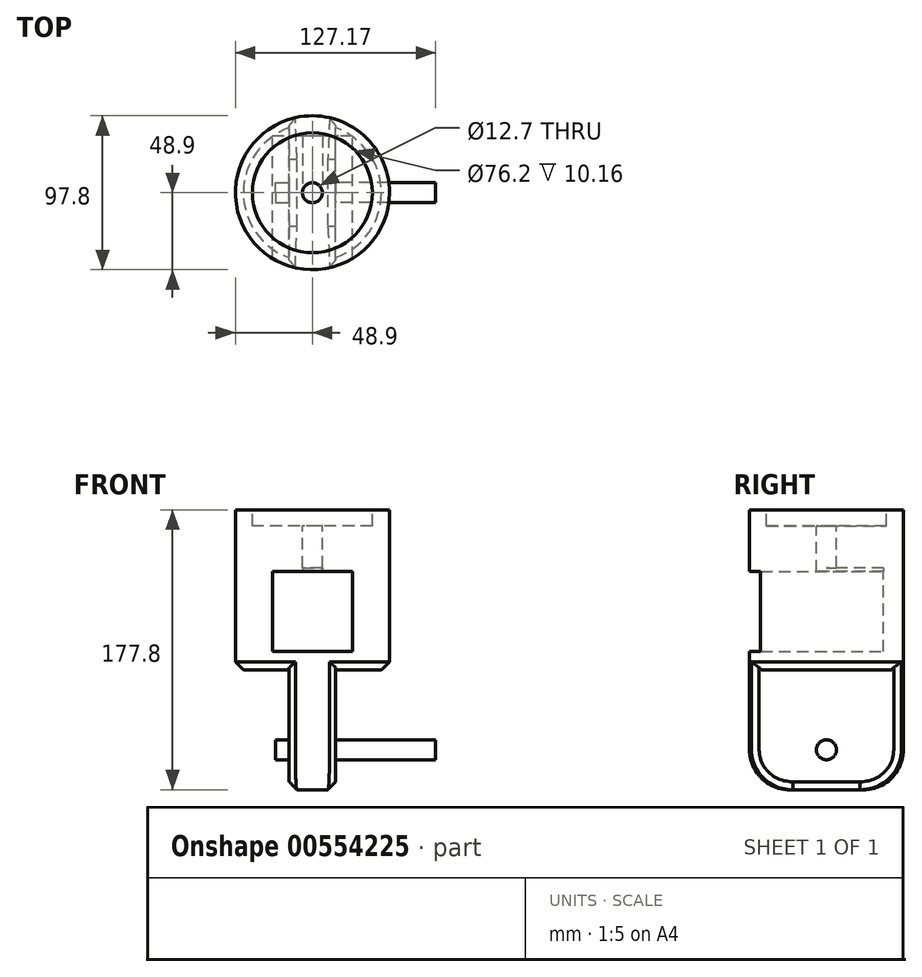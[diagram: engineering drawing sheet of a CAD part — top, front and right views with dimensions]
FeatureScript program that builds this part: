
annotation { "Feature Type Name" : "Feature", "Feature Type Description" : "" }
export const myFeature = defineFeature(function(context is Context, id is Id, definition is map)
    precondition{}
    {
        {
            var Q0;
            Q0=qCreatedBy(makeId("Top.planeOp"),FACE);
            var sketch = newSketch(context, id + "F0", { "sketchPlane" : qUnion([Q0])});
            skCircle(sketch, "E0", {"center": v(0, 0) * mm, "radius": 48.9 * mm});
            skSolve(sketch);
        }
        {
            var Q0;
            Q0=makeQuery(id+"F0.imprint","IMPRINT",FACE,{"disambiguationData":[TD([[makeQuery(id+"F0.imprint","IMPRINT",EDGE,{"derivedFrom":sQuery(id+"F0.wireOp",EDGE,"E0")}),1.0]])]});
            extrude(context, id + "F1", {"entities" : qUnion([Q0]), "depth" : 101.6 * mm, "offsetDistance" : 25.4 * mm});
        }
        {
            var Q0;
            Q0=makeQuery(id+"F1.opExtrude","CAP_FACE",FACE,{"disambiguationData":[OSD([sQuery(id+"F0.wireOp",EDGE,"E0")])],"isStart":true});
            var sketch = newSketch(context, id + "F2", { "sketchPlane" : qUnion([Q0])});
            skLineSegment(sketch, "E1.bottom", {"start": v(0, 43.76) * mm, "end": v(0, 43.76) * mm});
            skLineSegment(sketch, "E1.top", {"start": v(0, -43.76) * mm, "end": v(0, -43.76) * mm});
            skPoint(sketch, "E1.middle", {"position": v(0, 0) * mm});
            skLineSegment(sketch, "E2.bottom", {"start": v(14.77, 49.25) * mm, "end": v(-14.77, 49.25) * mm});
            skLineSegment(sketch, "E2.top", {"start": v(14.77, -49.25) * mm, "end": v(-14.77, -49.25) * mm});
            skLineSegment(sketch, "E2.left", {"start": v(14.77, 49.25) * mm, "end": v(14.77, -49.25) * mm});
            skLineSegment(sketch, "E2.right", {"start": v(-14.77, 49.25) * mm, "end": v(-14.77, -49.25) * mm});
            skSolve(sketch);
        }
        {
            var Q0;
            {var subQ0=sQuery(id+"F2.wireOp",EDGE,"E2.left");var subQ1=makeQuery(id+"F1.opExtrude","CAP_EDGE",EDGE,{"disambiguationData":[OSD([sQuery(id+"F0.wireOp",EDGE,"E0")])],"isStart":true});var subQ2=makeQuery(id+"F2.imprint","INTERSECT",VERTEX,{"disambiguationData":[OD(0.0)],"derivedFrom":[subQ1,subQ0]});Q0=makeQuery(id+"F2.imprint","IMPRINT",FACE,{"disambiguationData":[TD([[makeQuery(id+"F2.imprint","IMPRINT",EDGE,{"disambiguationData":[TD([[subQ2,-1.0]])],"derivedFrom":subQ0}),-1.0]])]});}
            extrude(context, id + "F3", {"entities" : qUnion([Q0]), "operationType" : NewBodyOperationType.ADD, "depth" : 76.2 * mm, "offsetDistance" : 25.4 * mm});
        }
        {
            var Q0;
            {var subQ0=sQuery(id+"F0.wireOp",EDGE,"E0");var subQ1=makeQuery(id+"F1.opExtrude","CAP_EDGE",EDGE,{"disambiguationData":[OSD([subQ0])],"isStart":true});Q0=makeQuery(id+"F3.opExtrude","CAP_EDGE",EDGE,{"disambiguationData":[OSD([subQ0]),TDD([makeQuery(id+"F2.imprint","IMPRINT",EDGE,{"disambiguationData":[TD([[makeQuery(id+"F2.imprint","INTERSECT",VERTEX,{"disambiguationData":[OD(1.0)],"derivedFrom":[subQ1,sQuery(id+"F2.wireOp",EDGE,"E2.left")]}),-1.0]])],"derivedFrom":subQ1})])],"isStart":false});}
            var Q1;
            {var subQ0=sQuery(id+"F0.wireOp",EDGE,"E0");var subQ1=makeQuery(id+"F1.opExtrude","CAP_EDGE",EDGE,{"disambiguationData":[OSD([subQ0])],"isStart":true});Q1=makeQuery(id+"F3.opExtrude","CAP_EDGE",EDGE,{"disambiguationData":[OSD([subQ0]),TDD([makeQuery(id+"F2.imprint","IMPRINT",EDGE,{"disambiguationData":[TD([[makeQuery(id+"F2.imprint","INTERSECT",VERTEX,{"disambiguationData":[OD(0.0)],"derivedFrom":[subQ1,sQuery(id+"F2.wireOp",EDGE,"E2.left")]}),1.0]])],"derivedFrom":subQ1})])],"isStart":false});}
            fillet(context, id + "F4", {"entities" : qUnion([Q0, Q1]), "radius" : 25.4 * mm, "tangentPropagation" : true, "allowEdgeOverflow" : false});
        }
        {
            var Q0;
            Q0=makeQuery(id+"F3.opExtrude","SWEPT_FACE",FACE,{"disambiguationData":[OSD([sQuery(id+"F2.wireOp",EDGE,"E2.left")])]});
            var sketch = newSketch(context, id + "F5", { "sketchPlane" : qUnion([Q0])});
            skLineSegment(sketch, "E3", {"start": v(0, 0) * mm, "end": v(0, -50.8) * mm});
            skPoint(sketch, "E3.endSnap0", {"position": v(0, 0) * mm});
            skCircle(sketch, "E4", {"center": v(0, -50.8) * mm, "radius": 6.35 * mm});
            skSolve(sketch);
        }
        {
            var Q0;
            Q0=makeQuery(id+"F5.imprint","IMPRINT",FACE,{"disambiguationData":[TD([[makeQuery(id+"F5.imprint","IMPRINT",EDGE,{"derivedFrom":sQuery(id+"F5.wireOp",EDGE,"E4")}),1.0]])]});
            extrude(context, id + "F6", {"entities" : qUnion([Q0]), "operationType" : NewBodyOperationType.ADD, "depth" : 63.5 * mm, "offsetDistance" : 25.4 * mm});
        }
        {
            var Q0;
            Q0=makeQuery(id+"F3.opExtrude","SWEPT_FACE",FACE,{"disambiguationData":[OSD([sQuery(id+"F2.wireOp",EDGE,"E2.right")])]});
            var sketch = newSketch(context, id + "F7", { "sketchPlane" : qUnion([Q0])});
            skLineSegment(sketch, "E5", {"start": v(0, 0) * mm, "end": v(0, -50.8) * mm});
            skPoint(sketch, "E5.endSnap0", {"position": v(0, 0) * mm});
            skCircle(sketch, "E6", {"center": v(0, -50.8) * mm, "radius": 6.35 * mm});
            skSolve(sketch);
        }
        {
            var Q0;
            Q0 = qSketchRegion(id + "F7", true);
            extrude(context, id + "F8", {"entities" : qUnion([Q0]), "operationType" : NewBodyOperationType.ADD, "depth" : 8.56 * mm, "offsetDistance" : 25.4 * mm});
        }
        {
            var Q0;
            Q0=makeQuery(id+"F1.opExtrude","CAP_FACE",FACE,{"disambiguationData":[OSD([sQuery(id+"F0.wireOp",EDGE,"E0")])],"isStart":false});
            var sketch = newSketch(context, id + "F9", { "sketchPlane" : qUnion([Q0])});
            skCircle(sketch, "E7", {"center": v(0, 0) * mm, "radius": 38.1 * mm});
            skSolve(sketch);
        }
        {
            var Q0;
            Q0=makeQuery(id+"F9.imprint","IMPRINT",FACE,{"disambiguationData":[TD([[makeQuery(id+"F9.imprint","IMPRINT",EDGE,{"derivedFrom":sQuery(id+"F9.wireOp",EDGE,"E7")}),1.0]])]});
            extrude(context, id + "F10", {"entities" : qUnion([Q0]), "operationType" : NewBodyOperationType.REMOVE, "oppositeDirection" : true, "depth" : 10.16 * mm, "offsetDistance" : 25.4 * mm});
        }
        {
            var Q0;
            Q0=makeQuery(id+"F10.boolean.opBoolean","COPY",FACE,{"derivedFrom":makeQuery(id+"F10.opExtrude","CAP_FACE",FACE,{"disambiguationData":[OSD([sQuery(id+"F9.wireOp",EDGE,"E7")])],"isStart":false})});
            var sketch = newSketch(context, id + "F11", { "sketchPlane" : qUnion([Q0])});
            skCircle(sketch, "E8", {"center": v(0, 0) * mm, "radius": 6.35 * mm});
            skSolve(sketch);
        }
        {
            var Q0;
            Q0 = qSketchRegion(id + "F11", true);
            extrude(context, id + "F12", {"entities" : qUnion([Q0]), "operationType" : NewBodyOperationType.ADD, "oppositeDirection" : true, "depth" : 50.8 * mm, "offsetDistance" : 25.4 * mm});
        }
        {
            var Q0;
            Q0=qCreatedBy(makeId("Front.planeOp"),FACE);
            var sketch = newSketch(context, id + "F13", { "sketchPlane" : qUnion([Q0])});
            skLineSegment(sketch, "E9.bottom", {"start": v(-25.4, 113.97) * mm, "end": v(25.4, 113.97) * mm});
            skLineSegment(sketch, "E9.top", {"start": v(-25.4, 177.05) * mm, "end": v(25.4, 177.05) * mm});
            skLineSegment(sketch, "E9.left", {"start": v(-25.4, 113.97) * mm, "end": v(-25.4, 177.05) * mm});
            skLineSegment(sketch, "E9.right", {"start": v(25.4, 113.97) * mm, "end": v(25.4, 177.05) * mm});
            skPoint(sketch, "E9.middle", {"position": v(0, 145.51) * mm});
            skSolve(sketch);
        }
        {
            var Q0;
            Q0 = qSketchRegion(id + "F13", true);
            extrude(context, id + "F14", {"entities" : qUnion([Q0]), "operationType" : NewBodyOperationType.REMOVE, "depth" : 90.68 * mm, "offsetDistance" : 25.4 * mm});
        }
        {
            var Q0;
            Q0 = qSketchRegion(id + "F13", true);
            extrude(context, id + "F15", {"entities" : qUnion([Q0]), "operationType" : NewBodyOperationType.REMOVE, "oppositeDirection" : true, "depth" : 24.13 * mm, "offsetDistance" : 25.4 * mm});
        }
        {
            var Q0;
            Q0 = qSketchRegion(id + "F11", true);
            extrude(context, id + "F16", {"entities" : qUnion([Q0]), "operationType" : NewBodyOperationType.REMOVE, "oppositeDirection" : true, "depth" : 41.4 * mm, "offsetDistance" : 25.4 * mm});
        }
        {
            var Q0;
            Q0=qCreatedBy(makeId("Front.planeOp"),FACE);
            var sketch = newSketch(context, id + "F17", { "sketchPlane" : qUnion([Q0])});
            skLineSegment(sketch, "E10.bottom", {"start": v(-25.4, 11.5) * mm, "end": v(25.4, 11.5) * mm});
            skLineSegment(sketch, "E10.top", {"start": v(-25.4, 62.3) * mm, "end": v(25.4, 62.3) * mm});
            skLineSegment(sketch, "E10.left", {"start": v(-25.4, 11.5) * mm, "end": v(-25.4, 62.3) * mm});
            skLineSegment(sketch, "E10.right", {"start": v(25.4, 11.5) * mm, "end": v(25.4, 62.3) * mm});
            skPoint(sketch, "E10.middle", {"position": v(0, 36.9) * mm});
            skSolve(sketch);
        }
        {
            var Q0;
            Q0 = qSketchRegion(id + "F17", true);
            extrude(context, id + "F18", {"entities" : qUnion([Q0]), "operationType" : NewBodyOperationType.REMOVE, "depth" : 80.52 * mm, "offsetDistance" : 25.4 * mm});
        }
        {
            var Q0;
            Q0=makeQuery(id+"F18.boolean.opBoolean","COPY",FACE,{"derivedFrom":makeQuery(id+"F18.opExtrude","CAP_FACE",FACE,{"disambiguationData":[OSD([sQuery(id+"F17.wireOp",EDGE,"E10.bottom"),sQuery(id+"F17.wireOp",EDGE,"E10.top"),sQuery(id+"F17.wireOp",EDGE,"E10.left"),sQuery(id+"F17.wireOp",EDGE,"E10.right")])],"isStart":true})});
            extrude(context, id + "F19", {"entities" : qUnion([Q0]), "operationType" : NewBodyOperationType.REMOVE, "oppositeDirection" : true, "depth" : 36.32 * mm, "offsetDistance" : 25.4 * mm});
        }
        {
            var Q0;
            {var subQ0=sQuery(id+"F17.wireOp",EDGE,"E10.right");var subQ1=sQuery(id+"F17.wireOp",EDGE,"E10.left");var subQ2=sQuery(id+"F17.wireOp",EDGE,"E10.top");var subQ3=sQuery(id+"F17.wireOp",EDGE,"E10.bottom");var subQ4=sQuery(id+"F11.wireOp",EDGE,"E8");Q0=makeQuery(id+"F19.boolean.opBoolean","COPY",FACE,{"derivedFrom":makeQuery(id+"F19.opExtrude","SWEPT_FACE",FACE,{"disambiguationData":[OSD([subQ4,subQ3,subQ2,subQ1,subQ0]),TDD([makeQuery(id+"F18.boolean.opBoolean","INTERSECT",EDGE,{"derivedFrom":[makeQuery(id+"F16.boolean.opBoolean","COPY",FACE,{"derivedFrom":makeQuery(id+"F16.opExtrude","CAP_FACE",FACE,{"disambiguationData":[OSD([subQ4])],"isStart":false})}),makeQuery(id+"F18.opExtrude","CAP_FACE",FACE,{"disambiguationData":[OSD([subQ3,subQ2,subQ1,subQ0])],"isStart":true})]})])]})});}
            extrude(context, id + "F20", {"entities" : qUnion([Q0]), "operationType" : NewBodyOperationType.REMOVE, "oppositeDirection" : true, "depth" : 14.73 * mm, "offsetDistance" : 25.4 * mm});
        }
        {
            var Q0;
            {var subQ0=sQuery(id+"F2.wireOp",EDGE,"E2.right");var subQ1=sQuery(id+"F0.wireOp",EDGE,"E0");var subQ2=makeQuery(id+"F1.opExtrude","CAP_EDGE",EDGE,{"disambiguationData":[OSD([subQ1])],"isStart":true});Q0=makeQuery(id+"F4.opFillet","BLEND_EDGE",EDGE,{"blendedFrom":[makeQuery(id+"F3.opExtrude","CAP_EDGE",EDGE,{"disambiguationData":[OSD([subQ1]),TDD([makeQuery(id+"F2.imprint","IMPRINT",EDGE,{"disambiguationData":[TD([[makeQuery(id+"F2.imprint","INTERSECT",VERTEX,{"disambiguationData":[OD(0.0)],"derivedFrom":[subQ2,sQuery(id+"F2.wireOp",EDGE,"E2.left")]}),1.0]])],"derivedFrom":subQ2})])],"isStart":false}),makeQuery(id+"F3.opExtrude","SWEPT_FACE",FACE,{"disambiguationData":[OSD([subQ0])]})],"blendedInto":[makeQuery(id+"F3.opExtrude","SWEPT_FACE",FACE,{"disambiguationData":[OSD([subQ0])]})]});}
            var Q1;
            {var subQ1=sQuery(id+"F0.wireOp",EDGE,"E0");var subQ2=makeQuery(id+"F1.opExtrude","CAP_EDGE",EDGE,{"disambiguationData":[OSD([subQ1])],"isStart":true});var subQ3=sQuery(id+"F2.wireOp",EDGE,"E2.right");Q1=makeQuery(id+"F3.boolean.opBoolean","SPLIT",EDGE,{"disambiguationData":[TD([makeQuery(id+"F3.opExtrude","SWEPT_FACE",FACE,{"disambiguationData":[OSD([subQ3])]})])],"derivedFrom":subQ2});}
            var Q2;
            {var subQ0=sQuery(id+"F2.wireOp",EDGE,"E2.left");var subQ1=sQuery(id+"F0.wireOp",EDGE,"E0");var subQ2=makeQuery(id+"F1.opExtrude","CAP_EDGE",EDGE,{"disambiguationData":[OSD([subQ1])],"isStart":true});Q2=makeQuery(id+"F3.boolean.opBoolean","SPLIT",EDGE,{"disambiguationData":[TD([makeQuery(id+"F3.opExtrude","SWEPT_FACE",FACE,{"disambiguationData":[OSD([subQ0])]})])],"derivedFrom":subQ2});}
            var Q3;
            {var subQ0=sQuery(id+"F2.wireOp",EDGE,"E2.left");var subQ1=sQuery(id+"F0.wireOp",EDGE,"E0");Q3=makeQuery(id+"F3.opExtrude","SWEPT_EDGE",EDGE,{"disambiguationData":[OSD([subQ1,subQ0]),TDD([makeQuery(id+"F2.imprint","INTERSECT",VERTEX,{"disambiguationData":[OD(0.0)],"derivedFrom":[makeQuery(id+"F1.opExtrude","CAP_EDGE",EDGE,{"disambiguationData":[OSD([subQ1])],"isStart":true}),subQ0]})])]});}
            chamfer(context, id + "F21", {"entities" : qUnion([Q0, Q1, Q2, Q3]), "width" : 5.08 * mm, "tangentPropagation" : true});
        }
    });
